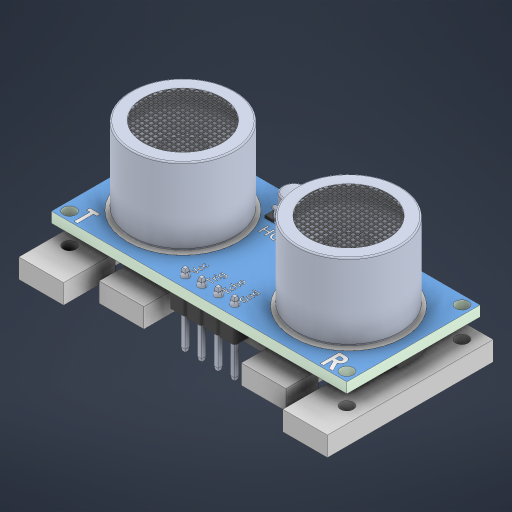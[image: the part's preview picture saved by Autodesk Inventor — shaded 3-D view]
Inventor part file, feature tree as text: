
AUTODESK INVENTOR PART (.ipt)
format: ipt  version: 2023 (Build 270158000, 158)  size: 8,358,912 bytes
history: native  units: mm
features: other x46, plane x1, extrude x1, sketch x1, projected_geometry x1
ambient origin geometry x8: Origin, YZ Plane, XZ Plane, XY Plane, X Axis, Y Axis, Z Axis, Center Point
bodies: Solid1 (feature_tree), Solid2 (feature_tree), Solid3 (feature_tree), Solid4 (feature_tree), Solid5 (feature_tree), Solid6 (feature_tree), Solid7 (feature_tree), Solid8 (feature_tree), Solid9 (feature_tree), Solid10 (feature_tree), Solid11 (feature_tree), Solid12 (feature_tree), Solid13 (feature_tree), Solid14 (feature_tree), Solid15 (feature_tree), Solid16 (feature_tree), Solid17 (feature_tree), Solid18 (feature_tree), Solid19 (feature_tree), Solid20 (feature_tree), Solid21 (feature_tree), Solid22 (feature_tree), Solid23 (feature_tree), Solid24 (feature_tree), Solid25 (feature_tree), Solid26 (feature_tree), Solid27 (feature_tree), Solid28 (feature_tree), Solid29 (feature_tree), Solid30 (feature_tree), Solid31 (feature_tree), Solid32 (feature_tree), Solid33 (feature_tree), Solid34 (feature_tree), Solid35 (feature_tree), Solid36 (feature_tree), Solid37 (feature_tree), Solid38 (feature_tree), Solid39 (feature_tree), Solid40 (feature_tree), Solid41 (feature_tree), Solid42 (feature_tree), Solid43 (feature_tree), Solid44 (feature_tree), Solid45 (feature_tree)
feature tree (50):
  other  "HC-SR04.iam"
  other  "HC-SR04board.ipt:1"
  other  "solder.ipt:1"
  other  "solder.ipt:2"
  other  "solder.ipt:3"
  other  "solder.ipt:4"
  other  "Emitter.ipt:1"
  other  "Emitter.ipt:2"
  other  "CrystalOscillator.ipt:1"
  other  "solder.ipt:5"
  other  "solder.ipt:6"
  other  "smdChip14pin.ipt:1"
  other  "smdChip14pin.ipt:2"
  other  "smdChip16pin.ipt:1"
  other  "smdceramiccapacitor.ipt:1"
  other  "smdceramiccapacitor.ipt:2"
  other  "smdceramiccapacitor.ipt:3"
  other  "smdceramiccapacitor.ipt:4"
  other  "smdceramiccapacitor.ipt:5"
  other  "smdceramiccapacitor.ipt:6"
  other  "smdceramiccapacitor.ipt:7"
  other  "smdResistor753.ipt:1"
  other  "smdResistor753.ipt:2"
  other  "smdResistor753.ipt:3"
  other  "smdResistor392.ipt:1"
  other  "smdResistor103.ipt:1"
  other  "smdResistor124.ipt:1"
  other  "smdResistor103.ipt:2"
  other  "smdResistor103.ipt:3"
  other  "smdResistor335.ipt:1"
  other  "smdResistor102.ipt:1"
  other  "smdResistor103.ipt:4"
  other  "smdResistor563.ipt:1"
  other  "smdResistor103.ipt:5"
  other  "smdResistor622.ipt:1"
  other  "smdResistor124.ipt:2"
  other  "smdResistor412.ipt:1"
  other  "smdResistor103.ipt:6"
  other  "solder.ipt:7"
  other  "solder.ipt:8"
  other  "solder.ipt:9"
  other  "solder.ipt:10"
  other  "headerMale.ipt:1"
  other  "headerMale.ipt:2"
  other  "headerMale.ipt:3"
  other  "headerMale.ipt:4"
  plane  "Work Plane1"
  extrude  "Extrusion1"  Depth=10.0mm
  sketch  "Sketch1"  dims[d0=10.0mm d1=3.0mm d2=5.0mm d3=15.0mm d4=1.0mm d5=6.0mm d6=2.5mm d7=10.0mm d8=5.1mm d9=2.1mm d10=3.0mm d11=0.0mm d12=3.0mm]
  projected_geometry  "Projected Loop1"
